# Revit family: CCTYP04
name_source: partatom
category: Furniture
units: mm (PartAtom-declared; Revit-internal decimal feet)

## family parameters
Always vertical = Yes
Cut with Voids When Loaded = No
OmniClass Number = 23.40.20.00
OmniClass Title = General Furniture and Specialties
Render Appearance Source = Family Geometry
Room Calculation Point = No
Shared = No
Work Plane-Based = No

## types (1)
- CCTYP04
    Cost = 20910 $
    Default Elevation = 0 mm  [stored 0 ft]
    Description = 2 x Devens Grey Side Chair, 1 x Auburn Gray Conference Chair - Express, 1 x 40 Led Task Light, W/ Dimmer & Transformer, 1 x Wall Mounted Open Overhead -16Hx72Wx14D, 1 x Height Adjustable Table 29"H W/Glides 30"X72" Top, 1 x Cbx Suspended Hat Modesty 12h For 72w (56 Actual), 2 x Cbx Full Depth Lat Bf 18dx21hx36w, 2 x Cbx Single Door Tower Hinge Left 18dx66hx12w, 1 x Cbx Tackboard Wall Mount 28hx72w
    Exported From CET Designer = Yes
    Manufacturer = AIS
    Model = 4667
    Show CCTYP04 = Yes
    VisibilityIndex = 0

note: [stored X ft] marks values corroborated as IEEE doubles in the binary element streams (Revit-internal decimal feet)

## geometry (parser evidence)
native form markers: Sweep x3
no freeform markers — native parametric forms only
